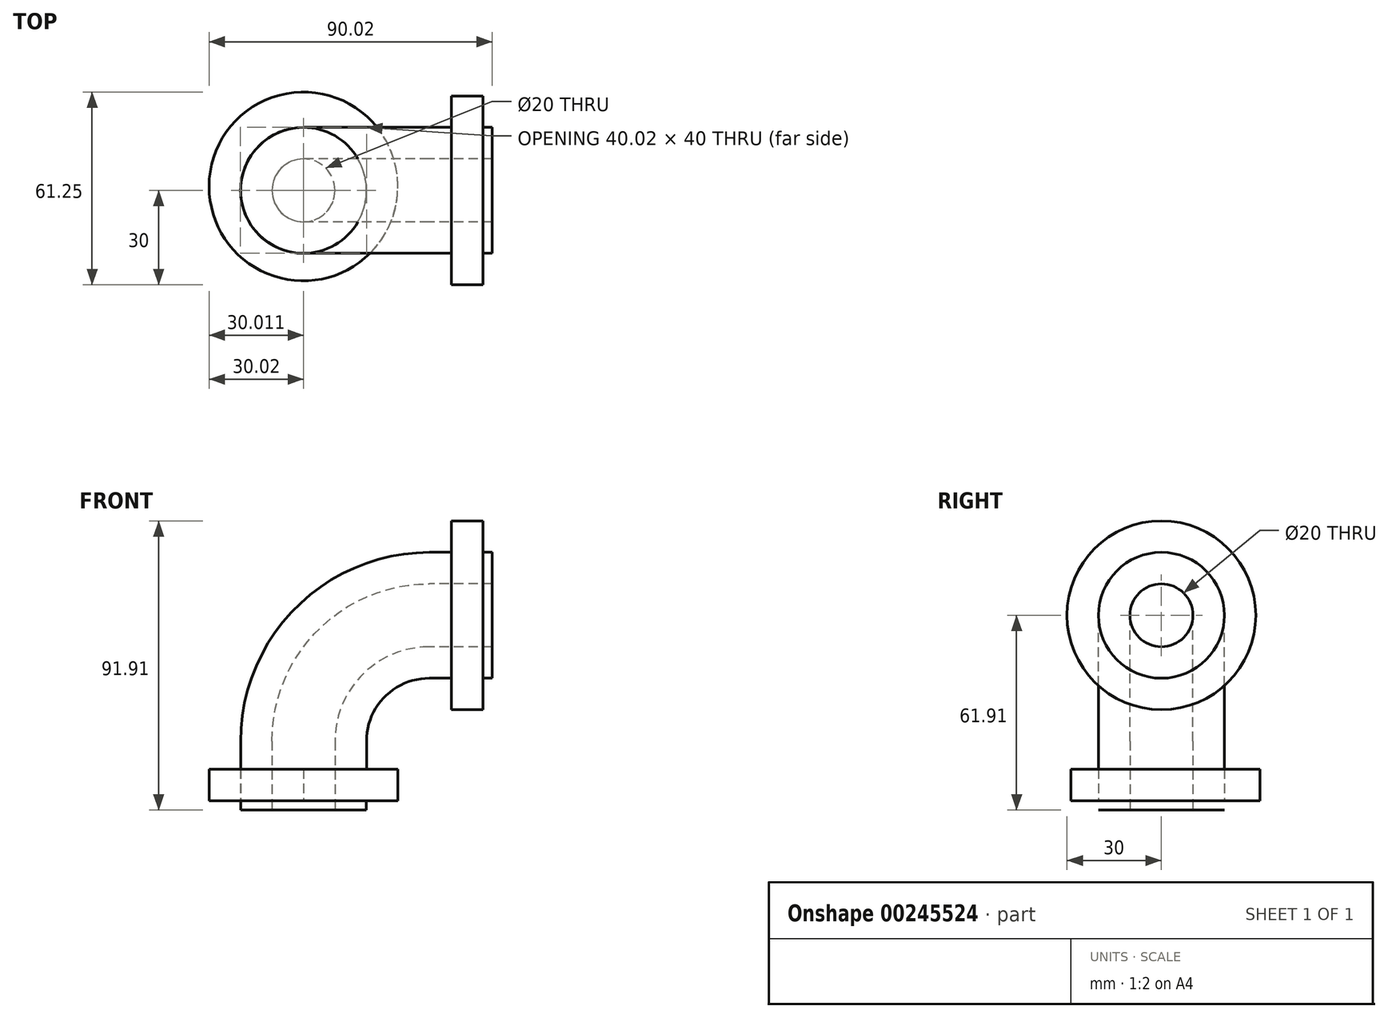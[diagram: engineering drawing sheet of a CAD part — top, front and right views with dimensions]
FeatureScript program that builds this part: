
annotation { "Feature Type Name" : "Feature", "Feature Type Description" : "" }
export const myFeature = defineFeature(function(context is Context, id is Id, definition is map)
    precondition{}
    {
        {
            var Q0;
            Q0=qCreatedBy(makeId("Right.planeOp"),FACE);
            var sketch = newSketch(context, id + "F0", { "sketchPlane" : qUnion([Q0])});
            skCircle(sketch, "E0", {"center": v(0, 0) * mm, "radius": 10 * mm});
            skCircle(sketch, "E1", {"center": v(0, 0) * mm, "radius": 20 * mm});
            skCircle(sketch, "E2", {"center": v(0, 0) * mm, "radius": 30 * mm});
            skSolve(sketch);
        }
        {
            var Q0;
            Q0=qCreatedBy(makeId("Front.planeOp"),FACE);
            var sketch = newSketch(context, id + "F1", { "sketchPlane" : qUnion([Q0])});
            skLineSegment(sketch, "E3.0", {"start": v(0, 30) * mm, "end": v(0, -30) * mm, "construction": true});
            skLineSegment(sketch, "E4.0", {"start": v(0, 20) * mm, "end": v(0, -20) * mm});
            skLineSegment(sketch, "E5.0", {"start": v(0, 10) * mm, "end": v(0, -10) * mm});
            skPoint(sketch, "E6.0", {"position": v(0, 0) * mm});
            skLineSegment(sketch, "E7", {"start": v(0, 20) * mm, "end": v(-20, 20) * mm});
            skLineSegment(sketch, "E8.MirrorCS", {"start": v(0, -20) * mm, "end": v(-20, -20) * mm});
            skLineSegment(sketch, "E9", {"start": v(-20, 20) * mm, "end": v(-20, 20) * mm});
            skLineSegment(sketch, "E10", {"start": v(-20, 32.94) * mm, "end": v(-20, -117.77) * mm, "construction": true});
            skArc(sketch, "E11", {"start": v(-20, 0) * mm, "mid": v(-48.28, -11.72) * mm, "end": v(-60, -40) * mm, "construction": true});
            skArc(sketch, "E12.0", {"start": v(-19.99, 20) * mm, "mid": v(-62.42, 2.43) * mm, "end": v(-80, -40) * mm});
            skArc(sketch, "E13.0", {"start": v(-20, -20) * mm, "mid": v(-34.14, -25.86) * mm, "end": v(-40, -40) * mm});
            skLineSegment(sketch, "E14", {"start": v(-20, -20) * mm, "end": v(-20, -20) * mm});
            skLineSegment(sketch, "E15", {"start": v(-6.18, -40) * mm, "end": v(-98.84, -40) * mm, "construction": true});
            skLineSegment(sketch, "E16", {"start": v(-80, -40) * mm, "end": v(-80, -61.9) * mm});
            skLineSegment(sketch, "E17", {"start": v(-80, -61.9) * mm, "end": v(-80, -61.9) * mm});
            skLineSegment(sketch, "E18", {"start": v(-60, -40) * mm, "end": v(-60, -76.03) * mm, "construction": true});
            skLineSegment(sketch, "E19.MirrorCS", {"start": v(-40, -40) * mm, "end": v(-40, -61.9) * mm});
            skLineSegment(sketch, "E20.MirrorCS", {"start": v(-40, -61.9) * mm, "end": v(-40, -61.9) * mm});
            skSolve(sketch);
        }
        {
            var Q0;
            Q0=makeQuery(id+"F0.imprint","IMPRINT",FACE,{"disambiguationData":[TD([[makeQuery(id+"F0.imprint","IMPRINT",EDGE,{"derivedFrom":sQuery(id+"F0.wireOp",EDGE,"E0")}),-1.0]])]});
            var Q1;
            Q1=sQuery(id+"F1.wireOp",EDGE,"E7");
            sweep(context, id + "F2", {"profiles" : qUnion([Q0]), "path" : qUnion([Q1])});
        }
        {
            var Q0;
            Q0=makeQuery(id+"F2.opSweep","CAP_FACE",FACE,{"disambiguationData":[OSD([sQuery(id+"F0.wireOp",EDGE,"E0"),sQuery(id+"F0.wireOp",EDGE,"E1"),sQuery(id+"F1.wireOp",VERTEX,"E7.end")])],"isStart":false});
            var Q1;
            Q1=sQuery(id+"F1.wireOp",EDGE,"E12.0");
            var Q2;
            Q2=sQuery(id+"F1.wireOp",EDGE,"E16");
            sweep(context, id + "F3", {"operationType" : NewBodyOperationType.ADD, "profiles" : qUnion([Q0]), "path" : qUnion([Q1, Q2])});
        }
        {
            var Q0;
            Q0=makeQuery(id+"F0.imprint","IMPRINT",FACE,{"disambiguationData":[TD([[makeQuery(id+"F0.imprint","IMPRINT",EDGE,{"derivedFrom":sQuery(id+"F0.wireOp",EDGE,"E1")}),-1.0]])]});
            extrude(context, id + "F4", {"entities" : qUnion([Q0]), "operationType" : NewBodyOperationType.ADD, "oppositeDirection" : true, "depth" : 13 * mm});
        }
        {
            var Q0;
            Q0=makeQuery(id+"F0.imprint","IMPRINT",FACE,{"disambiguationData":[TD([[makeQuery(id+"F0.imprint","IMPRINT",EDGE,{"derivedFrom":sQuery(id+"F0.wireOp",EDGE,"E1")}),-1.0]])]});
            extrude(context, id + "F5", {"entities" : qUnion([Q0]), "operationType" : NewBodyOperationType.REMOVE, "oppositeDirection" : true, "depth" : 3 * mm});
        }
        {
            var Q0;
            Q0=makeQuery(id+"F3.opSweep","CAP_FACE",FACE,{"disambiguationData":[OSD([sQuery(id+"F0.wireOp",EDGE,"E0"),sQuery(id+"F0.wireOp",EDGE,"E1"),sQuery(id+"F1.wireOp",VERTEX,"E7.end"),sQuery(id+"F1.wireOp",VERTEX,"E16.end")])],"isStart":false});
            cPlane(context, id + "F6", {"entities" : qUnion([Q0]), "cplaneType" : CPlaneType.OFFSET, "offset" : 0 * mm, "width" : 150 * mm, "height" : 150 * mm});
        }
        {
            var Q0;
            Q0=qCreatedBy(id+"F6.planeOp",FACE);
            var sketch = newSketch(context, id + "F7", { "sketchPlane" : qUnion([Q0])});
            skPoint(sketch, "E21.0", {"position": v(-60.02, 0) * mm});
            skCircle(sketch, "E22", {"center": v(-60.02, 0) * mm, "radius": 20 * mm});
            skCircle(sketch, "E23", {"center": v(-60.02, -1.25) * mm, "radius": 30 * mm});
            skSolve(sketch);
        }
        {
            var Q0;
            Q0=makeQuery(id+"F7.imprint","IMPRINT",FACE,{"disambiguationData":[TD([[makeQuery(id+"F7.imprint","IMPRINT",EDGE,{"derivedFrom":sQuery(id+"F7.wireOp",EDGE,"E22")}),-1.0]])]});
            extrude(context, id + "F8", {"entities" : qUnion([Q0]), "operationType" : NewBodyOperationType.ADD, "oppositeDirection" : true, "depth" : 13 * mm});
        }
        {
            var Q0;
            Q0=makeQuery(id+"F7.imprint","IMPRINT",FACE,{"disambiguationData":[TD([[makeQuery(id+"F7.imprint","IMPRINT",EDGE,{"derivedFrom":sQuery(id+"F7.wireOp",EDGE,"E22")}),-1.0]])]});
            extrude(context, id + "F9", {"entities" : qUnion([Q0]), "operationType" : NewBodyOperationType.REMOVE, "oppositeDirection" : true, "depth" : 3 * mm});
        }
    });
